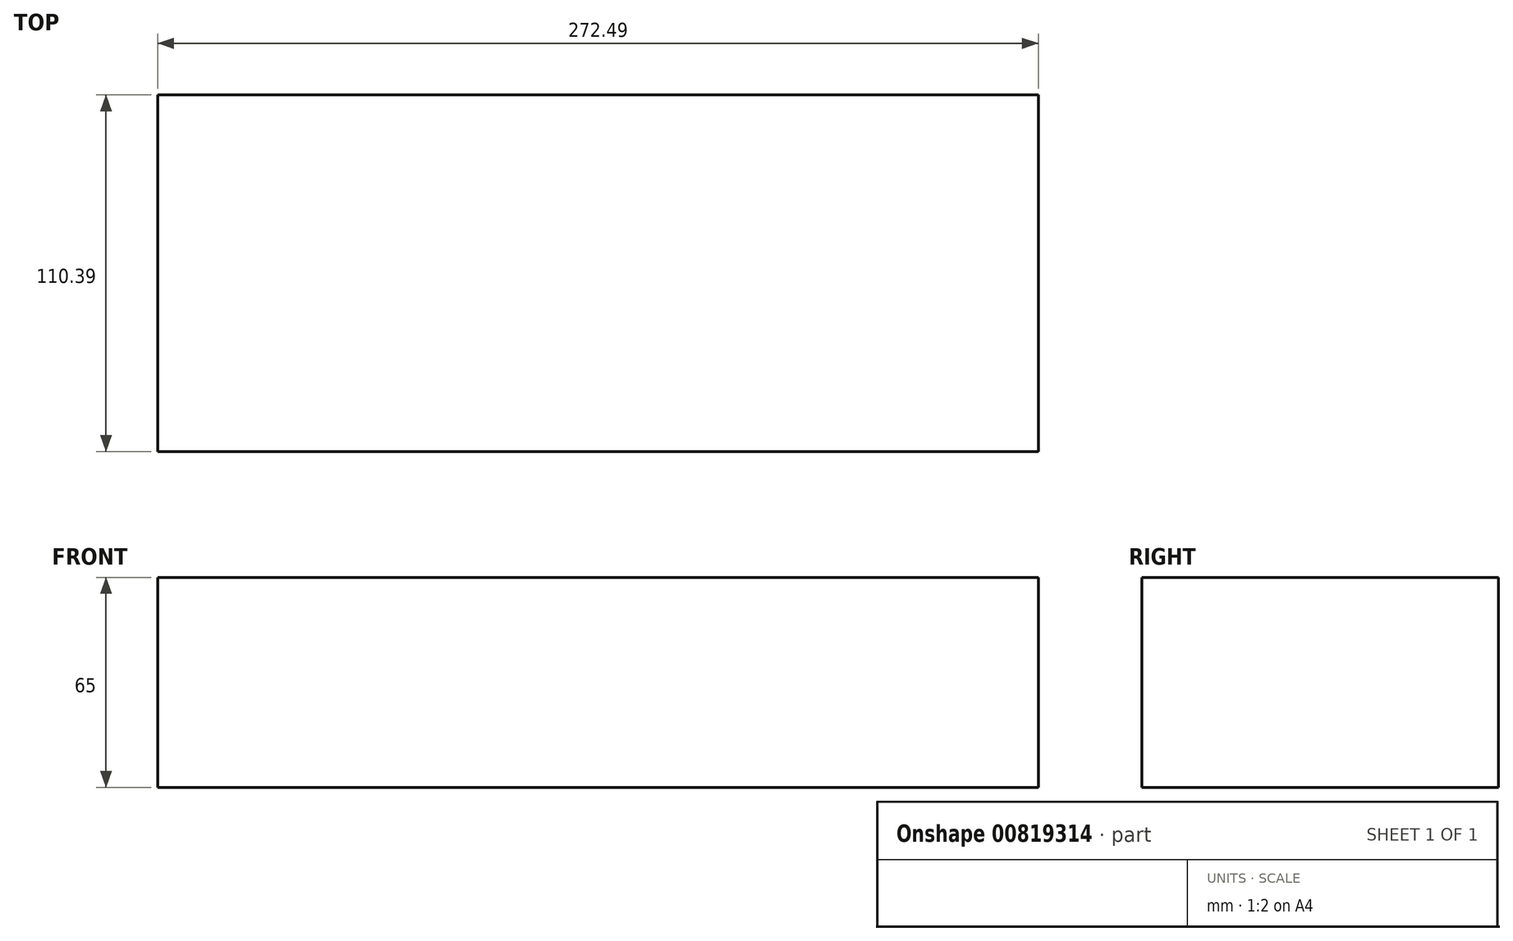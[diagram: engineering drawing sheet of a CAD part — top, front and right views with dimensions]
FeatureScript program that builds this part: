
annotation { "Feature Type Name" : "Feature", "Feature Type Description" : "" }
export const myFeature = defineFeature(function(context is Context, id is Id, definition is map)
    precondition{}
    {
        {
            var Q0;
            Q0=qCreatedBy(makeId("Top.planeOp"),FACE);
            var sketch = newSketch(context, id + "F0", { "sketchPlane" : qUnion([Q0])});
            skLineSegment(sketch, "E0.bottom", {"start": v(-154.17, 17.4) * mm, "end": v(118.32, 17.4) * mm});
            skLineSegment(sketch, "E0.top", {"start": v(-154.17, -92.98) * mm, "end": v(118.32, -92.98) * mm});
            skLineSegment(sketch, "E0.left", {"start": v(-154.17, 17.4) * mm, "end": v(-154.17, -92.98) * mm});
            skLineSegment(sketch, "E0.right", {"start": v(118.32, 17.4) * mm, "end": v(118.32, -92.98) * mm});
            skSolve(sketch);
        }
        {
            var Q0;
            Q0=makeQuery(id+"F0.imprint","IMPRINT",FACE,{"disambiguationData":[TD([[makeQuery(id+"F0.imprint","IMPRINT",EDGE,{"derivedFrom":sQuery(id+"F0.wireOp",EDGE,"E0.bottom")}),-1.0]])]});
            extrude(context, id + "F1", {"entities" : qUnion([Q0]), "depth" : 65 * mm, "offsetDistance" : 25 * mm});
        }
    });
